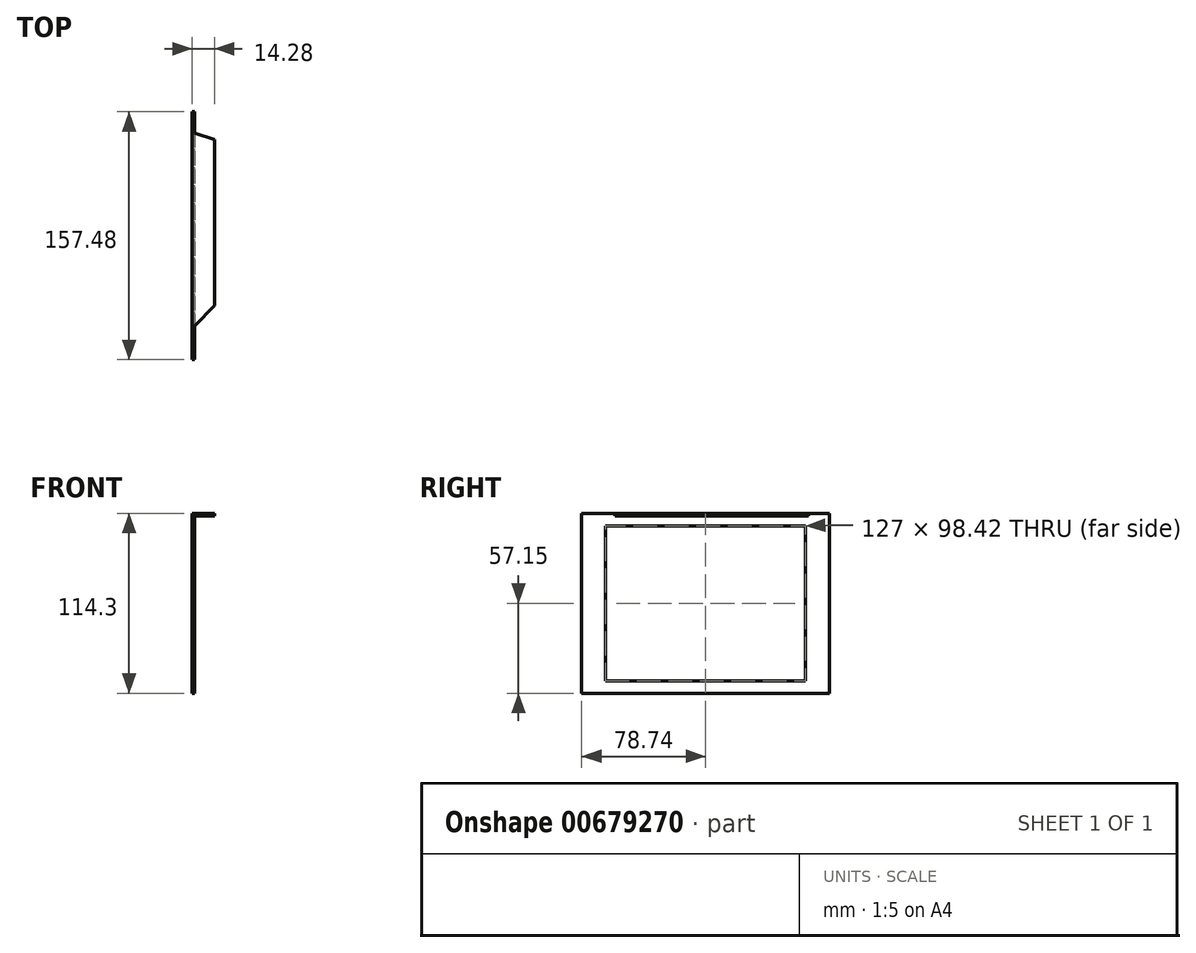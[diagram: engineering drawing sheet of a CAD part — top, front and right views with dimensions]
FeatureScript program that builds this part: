
annotation { "Feature Type Name" : "Feature", "Feature Type Description" : "" }
export const myFeature = defineFeature(function(context is Context, id is Id, definition is map)
    precondition{}
    {
        {
            var Q0;
            Q0=qCreatedBy(makeId("Top.planeOp"),FACE);
            var sketch = newSketch(context, id + "F0", { "sketchPlane" : qUnion([Q0])});
            skLineSegment(sketch, "E0.bottom", {"start": v(0.8, -78.74) * mm, "end": v(-0.8, -78.74) * mm});
            skLineSegment(sketch, "E0.top", {"start": v(0.8, 78.74) * mm, "end": v(-0.8, 78.74) * mm});
            skLineSegment(sketch, "E0.left", {"start": v(0.8, -78.74) * mm, "end": v(0.8, 78.74) * mm});
            skLineSegment(sketch, "E0.right", {"start": v(-0.8, -78.74) * mm, "end": v(-0.8, 78.74) * mm});
            skPoint(sketch, "E0.middle", {"position": v(0, 0) * mm});
            skSolve(sketch);
        }
        {
            var Q0;
            Q0=qSketchRegion(id+"F0",true);
            extrude(context, id + "F1", {"entities" : qUnion([Q0]), "depth" : 114.3 * mm});
        }
        {
            var Q0;
            Q0=makeQuery(id+"F1.opExtrude","SWEPT_FACE",FACE,{"disambiguationData":[OSD([sQuery(id+"F0.wireOp",EDGE,"E0.left")])]});
            var sketch = newSketch(context, id + "F2", { "sketchPlane" : qUnion([Q0])});
            skLineSegment(sketch, "E1.bottom", {"start": v(63.5, 106.36) * mm, "end": v(-63.5, 106.36) * mm});
            skLineSegment(sketch, "E1.top", {"start": v(63.5, 7.94) * mm, "end": v(-63.5, 7.94) * mm});
            skLineSegment(sketch, "E1.left", {"start": v(63.5, 106.36) * mm, "end": v(63.5, 7.94) * mm});
            skLineSegment(sketch, "E1.right", {"start": v(-63.5, 106.36) * mm, "end": v(-63.5, 7.94) * mm});
            skPoint(sketch, "E1.middle", {"position": v(0, 57.15) * mm});
            skPoint(sketch, "E1.middle.positionSnap0", {"position": v(-78.74, 57.15) * mm});
            skPoint(sketch, "E1.centerSnap0", {"position": v(-78.74, 57.15) * mm});
            skSolve(sketch);
        }
        {
            var Q0;
            Q0=qSketchRegion(id+"F2",true);
            extrude(context, id + "F3", {"entities" : qUnion([Q0]), "operationType" : NewBodyOperationType.REMOVE, "oppositeDirection" : true, "depth" : 25.4 * mm});
        }
        {
            var Q0;
            Q0=makeQuery(id+"F1.opExtrude","SWEPT_FACE",FACE,{"disambiguationData":[OSD([sQuery(id+"F0.wireOp",EDGE,"E0.left")])]});
            var sketch = newSketch(context, id + "F4", { "sketchPlane" : qUnion([Q0])});
            skPoint(sketch, "E2", {"position": v(-57.06, 114.3) * mm});
            skPoint(sketch, "E3", {"position": v(62.87, 114.3) * mm});
            skLineSegment(sketch, "E4.bottom", {"start": v(62.87, 114.3) * mm, "end": v(-57.06, 114.3) * mm});
            skLineSegment(sketch, "E4.top", {"start": v(62.87, 112.71) * mm, "end": v(-57.06, 112.71) * mm});
            skLineSegment(sketch, "E5.bottom", {"start": v(-57.06, 112.71) * mm, "end": v(-57.45, 112.71) * mm});
            skLineSegment(sketch, "E5.top", {"start": v(-57.06, 114.3) * mm, "end": v(-57.45, 114.3) * mm});
            skLineSegment(sketch, "E5.right", {"start": v(-57.45, 112.71) * mm, "end": v(-57.45, 114.3) * mm});
            skLineSegment(sketch, "E6.bottom", {"start": v(62.87, 112.71) * mm, "end": v(65.37, 112.71) * mm});
            skLineSegment(sketch, "E6.top", {"start": v(62.87, 114.3) * mm, "end": v(65.37, 114.3) * mm});
            skLineSegment(sketch, "E6.right", {"start": v(65.37, 112.71) * mm, "end": v(65.37, 114.3) * mm});
            skSolve(sketch);
        }
        {
            var Q0;
            Q0=qSketchRegion(id+"F4",true);
            extrude(context, id + "F5", {"entities" : qUnion([Q0]), "operationType" : NewBodyOperationType.ADD, "depth" : 12.7 * mm, "offsetDistance" : 25.4 * mm});
        }
        {
            var Q0;
            Q0=makeQuery(id+"F5.boolean.opBoolean","MERGE",FACE,{"derivedFrom":[makeQuery(id+"F1.opExtrude","CAP_FACE",FACE,{"disambiguationData":[OSD([sQuery(id+"F0.wireOp",EDGE,"E0.bottom"),sQuery(id+"F0.wireOp",EDGE,"E0.top"),sQuery(id+"F0.wireOp",EDGE,"E0.left"),sQuery(id+"F0.wireOp",EDGE,"E0.right")])],"isStart":false}),makeQuery(id+"F5.opExtrude","SWEPT_FACE",FACE,{"disambiguationData":[OSD([sQuery(id+"F4.wireOp",EDGE,"E4.bottom"),sQuery(id+"F4.wireOp",EDGE,"E5.top"),sQuery(id+"F4.wireOp",EDGE,"E6.top")])]})]});
            var sketch = newSketch(context, id + "F6", { "sketchPlane" : qUnion([Q0])});
            skLineSegment(sketch, "E7", {"start": v(0.8, 65.37) * mm, "end": v(13.5, 60.97) * mm});
            skLineSegment(sketch, "E8", {"start": v(13.5, 60.97) * mm, "end": v(13.5, 65.37) * mm});
            skLineSegment(sketch, "E9", {"start": v(13.5, 65.37) * mm, "end": v(0.8, 65.37) * mm});
            skLineSegment(sketch, "E10", {"start": v(0.8, -57.45) * mm, "end": v(13.5, -44.28) * mm});
            skLineSegment(sketch, "E11", {"start": v(13.5, -44.28) * mm, "end": v(13.5, -57.45) * mm});
            skLineSegment(sketch, "E12", {"start": v(13.5, -57.45) * mm, "end": v(0.8, -57.45) * mm});
            skSolve(sketch);
        }
        {
            var Q0;
            Q0 = qSketchRegion(id + "F6", true);
            extrude(context, id + "F7", {"entities" : qUnion([Q0]), "operationType" : NewBodyOperationType.REMOVE, "oppositeDirection" : true, "depth" : 25.4 * mm, "offsetDistance" : 25.4 * mm});
        }
    });
